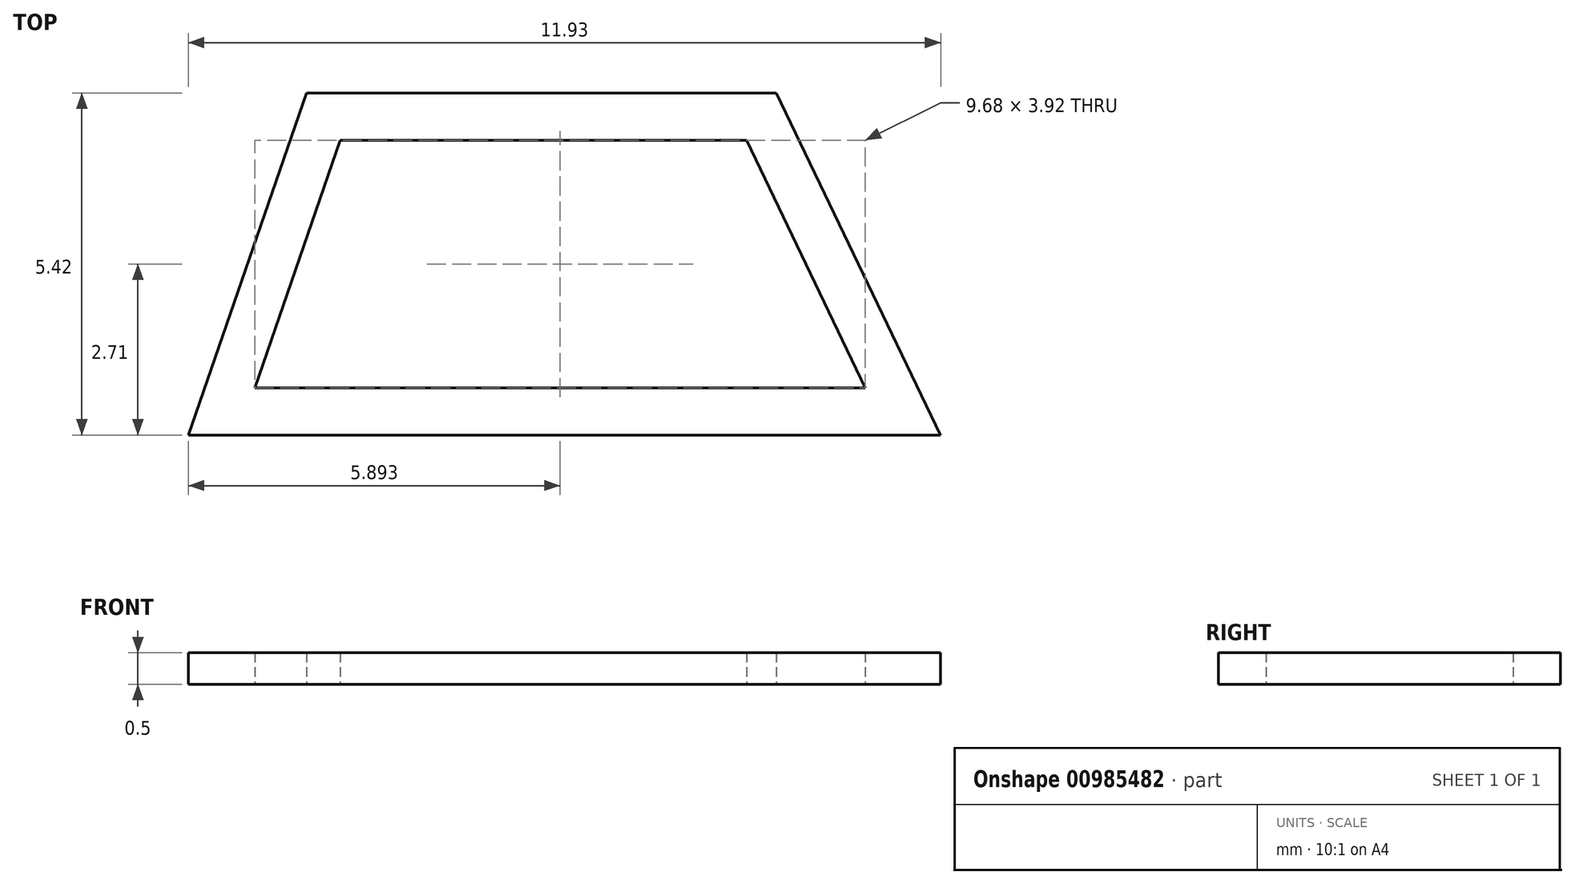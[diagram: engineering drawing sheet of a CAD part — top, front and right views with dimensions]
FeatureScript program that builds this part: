
annotation { "Feature Type Name" : "Feature", "Feature Type Description" : "" }
export const myFeature = defineFeature(function(context is Context, id is Id, definition is map)
    precondition{}
    {
        {
            var Q0;
            Q0=qCreatedBy(makeId("Top.planeOp"),FACE);
            var sketch = newSketch(context, id + "F0", { "sketchPlane" : qUnion([Q0])});
            skLineSegment(sketch, "E0", {"start": v(0, 0) * mm, "end": v(11.93, 0) * mm});
            skLineSegment(sketch, "E1", {"start": v(0, 0) * mm, "end": v(1.87, 5.42) * mm});
            skLineSegment(sketch, "E2", {"start": v(1.87, 5.42) * mm, "end": v(9.32, 5.42) * mm});
            skLineSegment(sketch, "E3", {"start": v(9.32, 5.42) * mm, "end": v(11.93, 0) * mm});
            skLineSegment(sketch, "E4", {"start": v(1.05, 0.75) * mm, "end": v(2.4, 4.67) * mm});
            skLineSegment(sketch, "E5", {"start": v(2.4, 4.67) * mm, "end": v(8.85, 4.67) * mm});
            skLineSegment(sketch, "E6", {"start": v(8.85, 4.67) * mm, "end": v(10.73, 0.75) * mm});
            skLineSegment(sketch, "E7", {"start": v(10.73, 0.75) * mm, "end": v(1.05, 0.75) * mm});
            skSolve(sketch);
        }
        {
            var Q0;
            Q0=qSketchRegion(id+"F0",true);
            extrude(context, id + "F1", {"entities" : qUnion([Q0]), "depth" : .5 * mm});
        }
    });
